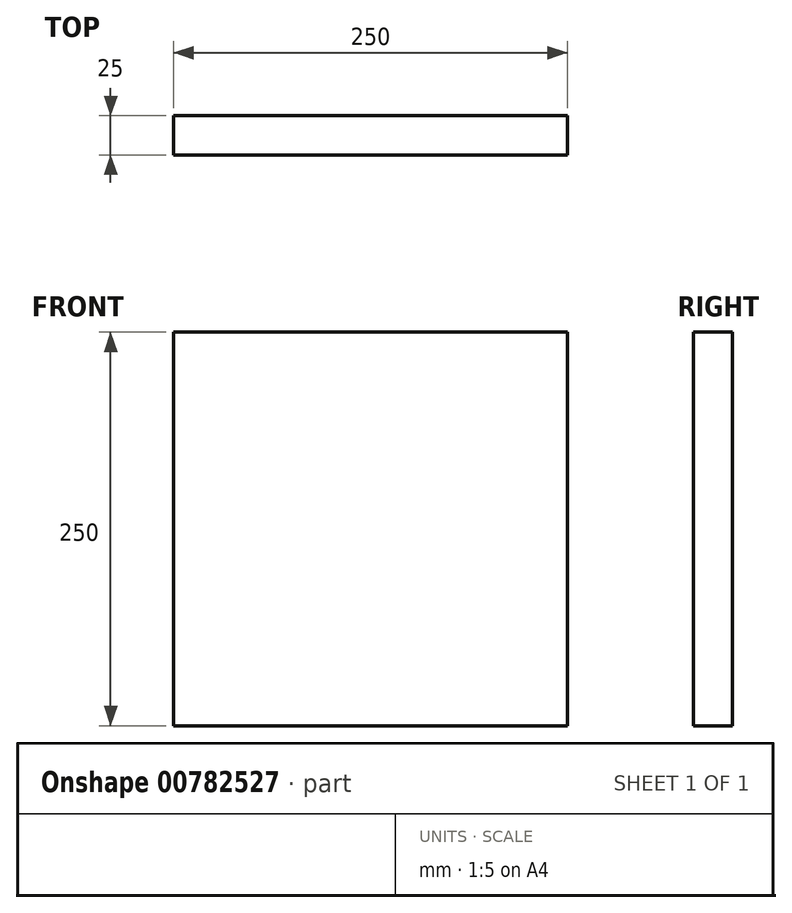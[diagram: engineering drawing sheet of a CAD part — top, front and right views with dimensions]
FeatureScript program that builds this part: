
annotation { "Feature Type Name" : "Feature", "Feature Type Description" : "" }
export const myFeature = defineFeature(function(context is Context, id is Id, definition is map)
    precondition{}
    {
        {
            var Q0;
            Q0=qCreatedBy(makeId("Front.planeOp"),FACE);
            var sketch = newSketch(context, id + "F0", { "sketchPlane" : qUnion([Q0])});
            skLineSegment(sketch, "E0.bottom", {"start": v(-121.85, 125.04) * mm, "end": v(128.15, 125.04) * mm});
            skLineSegment(sketch, "E0.top", {"start": v(-121.85, -124.96) * mm, "end": v(128.15, -124.96) * mm});
            skLineSegment(sketch, "E0.left", {"start": v(-121.85, 125.04) * mm, "end": v(-121.85, -124.96) * mm});
            skLineSegment(sketch, "E0.right", {"start": v(128.15, 125.04) * mm, "end": v(128.15, -124.96) * mm});
            skSolve(sketch);
        }
        {
            var Q0;
            Q0=makeQuery(id+"F0.imprint","IMPRINT",FACE,{"disambiguationData":[TD([[makeQuery(id+"F0.imprint","IMPRINT",EDGE,{"derivedFrom":sQuery(id+"F0.wireOp",EDGE,"E0.bottom")}),-1.0]])]});
            extrude(context, id + "F1", {"entities" : qUnion([Q0]), "depth" : 25 * mm, "offsetDistance" : 25 * mm});
        }
    });
